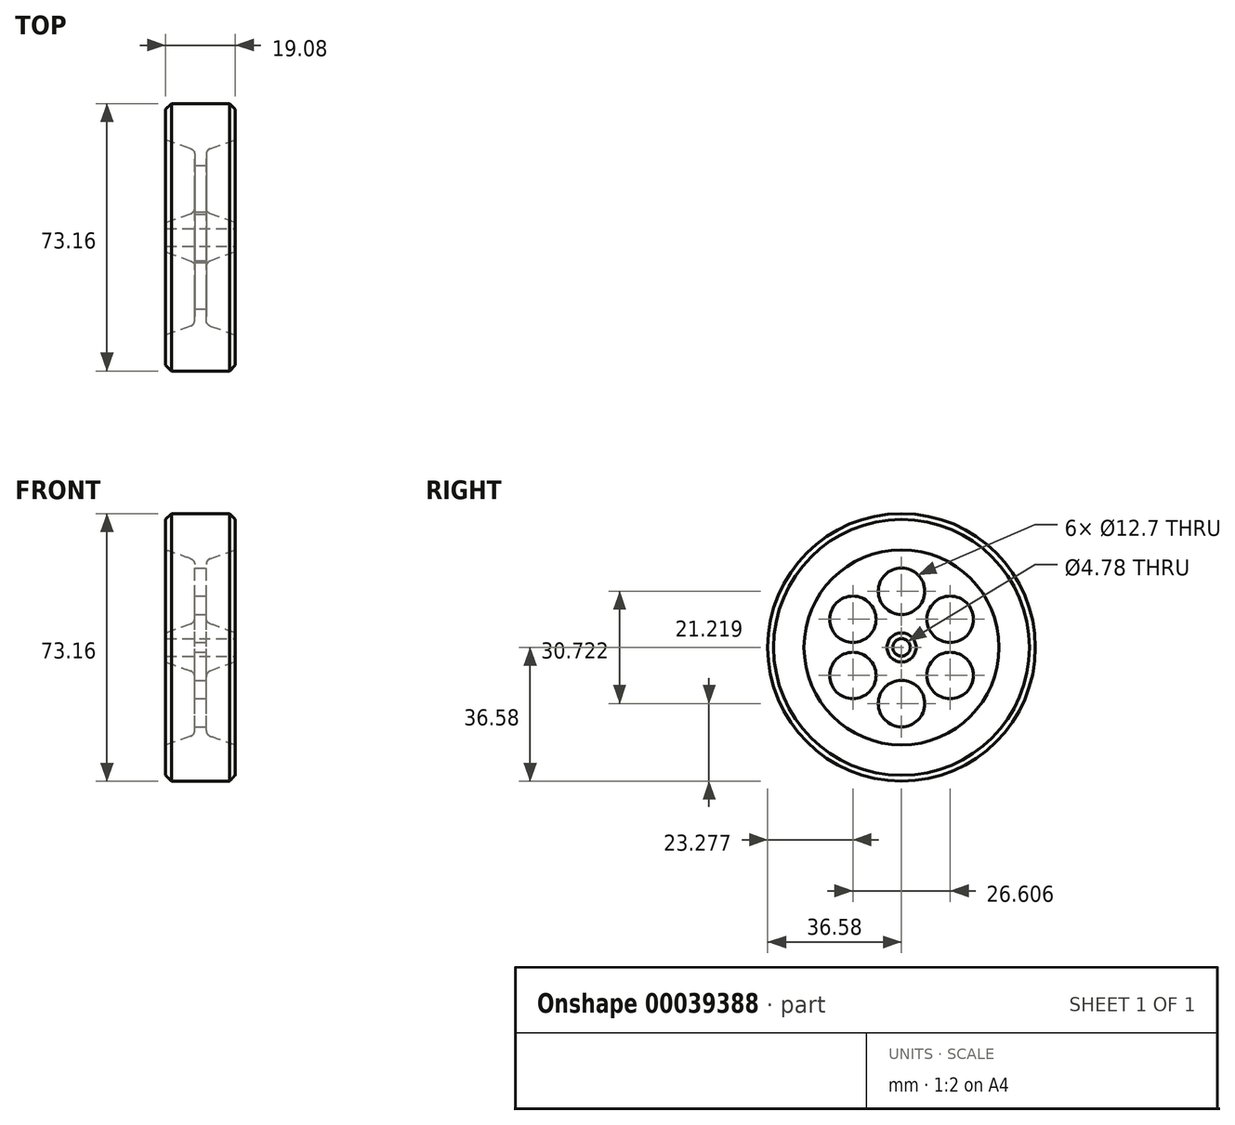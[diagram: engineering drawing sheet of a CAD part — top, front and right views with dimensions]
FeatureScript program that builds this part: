
annotation { "Feature Type Name" : "Feature", "Feature Type Description" : "" }
export const myFeature = defineFeature(function(context is Context, id is Id, definition is map)
    precondition{}
    {
        {
            var Q0;
            Q0=qCreatedBy(makeId("Front.planeOp"),FACE);
            var sketch = newSketch(context, id + "F0", { "sketchPlane" : qUnion([Q0])});
            skLineSegment(sketch, "E0.bottom", {"start": v(-19.06, 0) * mm, "end": v(0, 0) * mm});
            skLineSegment(sketch, "E0.top", {"start": v(-19.08, 36.58) * mm, "end": v(0, 36.58) * mm});
            skLineSegment(sketch, "E1", {"start": v(0, 36.58) * mm, "end": v(0, 26.67) * mm});
            skLineSegment(sketch, "E2", {"start": v(0, 3.98) * mm, "end": v(0, 0) * mm});
            skLineSegment(sketch, "E3", {"start": v(-19.08, 36.58) * mm, "end": v(-19.08, 26.67) * mm});
            skLineSegment(sketch, "E4", {"start": v(-19.08, 26.67) * mm, "end": v(-11.13, 23.88) * mm});
            skLineSegment(sketch, "E5", {"start": v(-11.13, 23.88) * mm, "end": v(-11.13, 6.86) * mm});
            skLineSegment(sketch, "E6", {"start": v(-11.13, 6.86) * mm, "end": v(-19.06, 3.98) * mm});
            skLineSegment(sketch, "E7", {"start": v(-19.06, 3.98) * mm, "end": v(-19.06, 0) * mm});
            skLineSegment(sketch, "E8", {"start": v(0, 26.67) * mm, "end": v(-7.95, 23.88) * mm});
            skLineSegment(sketch, "E9", {"start": v(-7.95, 23.88) * mm, "end": v(-7.95, 6.86) * mm});
            skLineSegment(sketch, "E10", {"start": v(0, 3.98) * mm, "end": v(-7.95, 6.86) * mm});
            skSolve(sketch);
        }
        {
            var Q0;
            Q0=makeQuery(id+"F0.imprint","IMPRINT",FACE,{"disambiguationData":[TD([[makeQuery(id+"F0.imprint","IMPRINT",EDGE,{"derivedFrom":sQuery(id+"F0.wireOp",EDGE,"E0.bottom")}),1.0]])]});
            var Q1;
            Q1=sQuery(id+"F0.wireOp",EDGE,"E0.bottom");
            revolve(context, id + "F1", {"entities" : qUnion([Q0]), "axis" : qUnion([Q1]), "revolveType" : RevolveType.FULL});
        }
        {
            var Q0;
            Q0=makeQuery(id+"F1.opRevolve","SWEPT_FACE",FACE,{"disambiguationData":[OSD([sQuery(id+"F0.wireOp",EDGE,"E2")])]});
            var sketch = newSketch(context, id + "F2", { "sketchPlane" : qUnion([Q0])});
            skCircle(sketch, "E11", {"center": v(0, 0) * mm, "radius": 2.39 * mm});
            skSolve(sketch);
        }
        {
            var Q0;
            Q0=makeQuery(id+"F2.imprint","IMPRINT",FACE,{"disambiguationData":[TD([[makeQuery(id+"F2.imprint","IMPRINT",EDGE,{"derivedFrom":sQuery(id+"F2.wireOp",EDGE,"E11")}),1.0]])]});
            extrude(context, id + "F3", {"entities" : qUnion([Q0]), "operationType" : NewBodyOperationType.REMOVE, "endBound" : BoundingType.THROUGH_ALL, "oppositeDirection" : true, "depth" : 25.4 * mm});
        }
        {
            var Q0;
            Q0=makeQuery(id+"F1.opRevolve","SWEPT_EDGE",EDGE,{"disambiguationData":[OSD([sQuery(id+"F0.wireOp",EDGE,"E0.top"),sQuery(id+"F0.wireOp",EDGE,"E1")])]});
            var Q1;
            Q1=makeQuery(id+"F1.opRevolve","SWEPT_EDGE",EDGE,{"disambiguationData":[OSD([sQuery(id+"F0.wireOp",EDGE,"E0.top"),sQuery(id+"F0.wireOp",EDGE,"E3")])]});
            chamfer(context, id + "F4", {"entities" : qUnion([Q0, Q1]), "width" : 1.6 * mm, "tangentPropagation" : true});
        }
        {
            var Q0;
            Q0=makeQuery(id+"F1.opRevolve","SWEPT_EDGE",EDGE,{"disambiguationData":[OSD([sQuery(id+"F0.wireOp",EDGE,"E8"),sQuery(id+"F0.wireOp",EDGE,"E9")])]});
            var Q1;
            Q1=makeQuery(id+"F1.opRevolve","SWEPT_EDGE",EDGE,{"disambiguationData":[OSD([sQuery(id+"F0.wireOp",EDGE,"E4"),sQuery(id+"F0.wireOp",EDGE,"E5")])]});
            var Q2;
            Q2=makeQuery(id+"F1.opRevolve","SWEPT_EDGE",EDGE,{"disambiguationData":[OSD([sQuery(id+"F0.wireOp",EDGE,"E9"),sQuery(id+"F0.wireOp",EDGE,"E10")])]});
            var Q3;
            Q3=makeQuery(id+"F1.opRevolve","SWEPT_EDGE",EDGE,{"disambiguationData":[OSD([sQuery(id+"F0.wireOp",EDGE,"E5"),sQuery(id+"F0.wireOp",EDGE,"E6")])]});
            fillet(context, id + "F5", {"entities" : qUnion([Q0, Q1, Q2, Q3]), "radius" : 1.6 * mm, "tangentPropagation" : true, "allowEdgeOverflow" : false});
        }
        {
            var Q0;
            Q0=makeQuery(id+"F1.opRevolve","SWEPT_FACE",FACE,{"disambiguationData":[OSD([sQuery(id+"F0.wireOp",EDGE,"E9")])]});
            var sketch = newSketch(context, id + "F6", { "sketchPlane" : qUnion([Q0])});
            skCircle(sketch, "E12", {"center": v(0, 15.36) * mm, "radius": 6.35 * mm});
            skPoint(sketch, "E13.orphan", {"position": v(0, 22.74) * mm});
            skPoint(sketch, "E14.start.orphan", {"position": v(0, 7.98) * mm});
            skCircle(sketch, "E15.1.0", {"center": v(-13.3, 7.68) * mm, "radius": 6.35 * mm});
            skCircle(sketch, "E15.2.0", {"center": v(-13.3, -7.68) * mm, "radius": 6.35 * mm});
            skCircle(sketch, "E15.3.0", {"center": v(0, -15.36) * mm, "radius": 6.35 * mm});
            skCircle(sketch, "E15.4.0", {"center": v(13.3, -7.68) * mm, "radius": 6.35 * mm});
            skCircle(sketch, "E15.5.0", {"center": v(13.3, 7.68) * mm, "radius": 6.35 * mm});
            skPoint(sketch, "E15.center", {"position": v(0, 0) * mm});
            skSolve(sketch);
        }
        {
            var Q0;
            Q0=makeQuery(id+"F6.imprint","IMPRINT",FACE,{"disambiguationData":[TD([[makeQuery(id+"F6.imprint","IMPRINT",EDGE,{"derivedFrom":sQuery(id+"F6.wireOp",EDGE,"E12")}),1.0]])]});
            var Q1;
            Q1=makeQuery(id+"F6.imprint","IMPRINT",FACE,{"disambiguationData":[TD([[makeQuery(id+"F6.imprint","IMPRINT",EDGE,{"derivedFrom":sQuery(id+"F6.wireOp",EDGE,"E15.1.0")}),1.0]])]});
            var Q2;
            Q2=makeQuery(id+"F6.imprint","IMPRINT",FACE,{"disambiguationData":[TD([[makeQuery(id+"F6.imprint","IMPRINT",EDGE,{"derivedFrom":sQuery(id+"F6.wireOp",EDGE,"E15.2.0")}),1.0]])]});
            var Q3;
            Q3=makeQuery(id+"F6.imprint","IMPRINT",FACE,{"disambiguationData":[TD([[makeQuery(id+"F6.imprint","IMPRINT",EDGE,{"derivedFrom":sQuery(id+"F6.wireOp",EDGE,"E15.3.0")}),1.0]])]});
            var Q4;
            Q4=makeQuery(id+"F6.imprint","IMPRINT",FACE,{"disambiguationData":[TD([[makeQuery(id+"F6.imprint","IMPRINT",EDGE,{"derivedFrom":sQuery(id+"F6.wireOp",EDGE,"E15.4.0")}),1.0]])]});
            var Q5;
            Q5=makeQuery(id+"F6.imprint","IMPRINT",FACE,{"disambiguationData":[TD([[makeQuery(id+"F6.imprint","IMPRINT",EDGE,{"derivedFrom":sQuery(id+"F6.wireOp",EDGE,"E15.5.0")}),1.0]])]});
            extrude(context, id + "F7", {"entities" : qUnion([Q0, Q1, Q2, Q3, Q4, Q5]), "operationType" : NewBodyOperationType.REMOVE, "endBound" : BoundingType.THROUGH_ALL, "oppositeDirection" : true, "depth" : 25.4 * mm});
        }
    });
